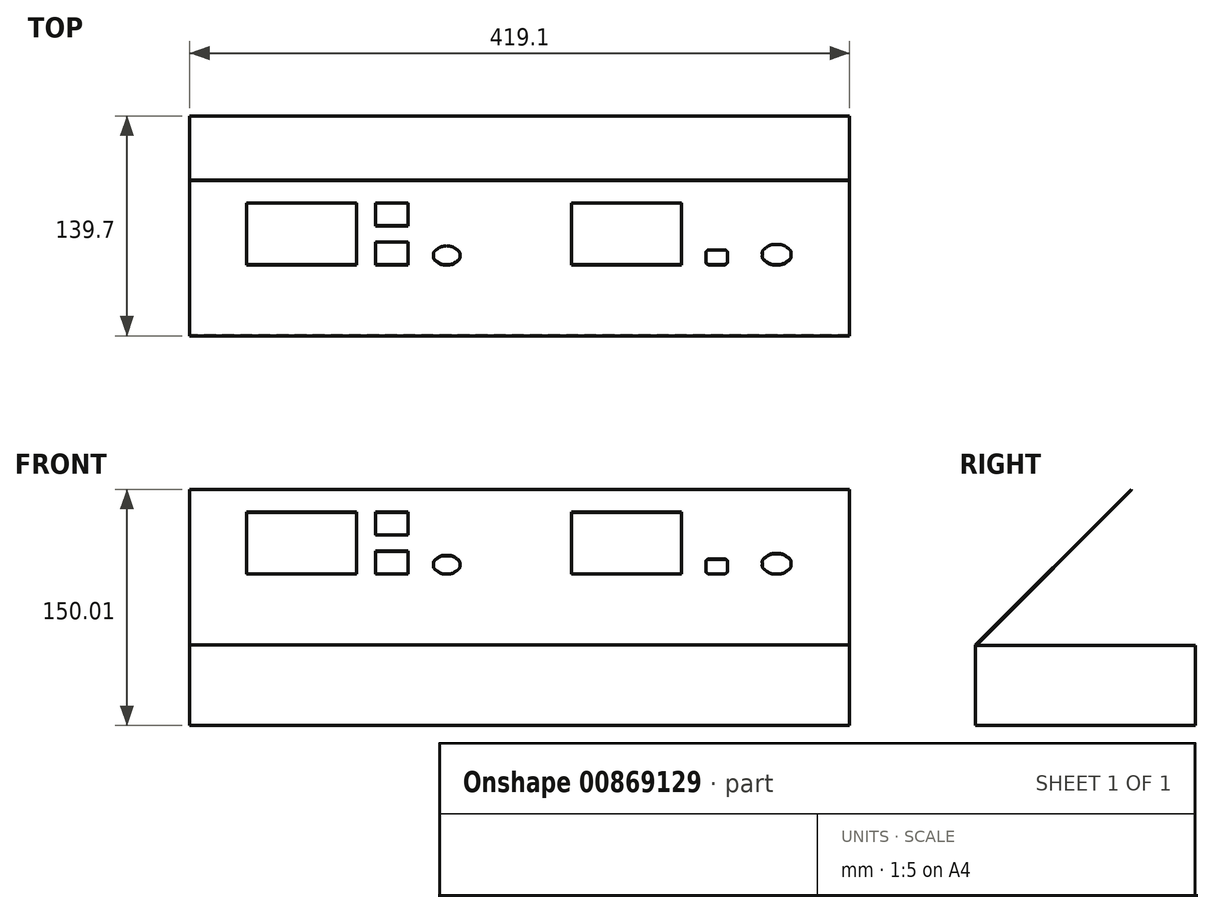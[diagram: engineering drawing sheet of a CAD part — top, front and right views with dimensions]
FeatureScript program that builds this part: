
annotation { "Feature Type Name" : "Feature", "Feature Type Description" : "" }
export const myFeature = defineFeature(function(context is Context, id is Id, definition is map)
    precondition{}
    {
        {
            var Q0;
            Q0=qCreatedBy(makeId("Right.planeOp"),FACE);
            var sketch = newSketch(context, id + "F0", { "sketchPlane" : qUnion([Q0])});
            skLineSegment(sketch, "E0.bottom", {"start": v(0, 0) * mm, "end": v(-139.7, 0) * mm});
            skLineSegment(sketch, "E0.top", {"start": v(0, 50.8) * mm, "end": v(-139.3, 50.8) * mm});
            skLineSegment(sketch, "E0.left", {"start": v(0, 0) * mm, "end": v(0, 50.8) * mm});
            skLineSegment(sketch, "E0.right", {"start": v(-139.7, 0) * mm, "end": v(-139.7, 51.22) * mm});
            skLineSegment(sketch, "E1", {"start": v(-139.7, 51.22) * mm, "end": v(-40.92, 150) * mm});
            skLineSegment(sketch, "E2", {"start": v(-40.92, 150) * mm, "end": v(-40.63, 149.72) * mm});
            skLineSegment(sketch, "E3", {"start": v(-40.63, 149.72) * mm, "end": v(-139.3, 51.05) * mm});
            skLineSegment(sketch, "E4", {"start": v(-139.3, 50.8) * mm, "end": v(-139.3, 51.05) * mm});
            skLineSegment(sketch, "E5", {"start": v(-139.3, 50.8) * mm, "end": v(-139.7, 50.8) * mm, "construction": true});
            skSolve(sketch);
        }
        {
            var Q0;
            Q0=qSketchRegion(id+"F0",true);
            extrude(context, id + "F1", {"entities" : qUnion([Q0]), "endBound" : BoundingType.SYMMETRIC, "depth" : 419.1 * mm, "offsetDistance" : 25.4 * mm});
        }
        {
            var Q0;
            Q0=makeQuery(id+"F1.opExtrude","SWEPT_FACE",FACE,{"disambiguationData":[OSD([sQuery(id+"F0.wireOp",EDGE,"E1")])]});
            var sketch = newSketch(context, id + "F2", { "sketchPlane" : qUnion([Q0])});
            skLineSegment(sketch, "E6", {"start": v(118.3, 12.35) * mm, "end": v(118.3, 3.62) * mm});
            skLineSegment(sketch, "E7", {"start": v(-173.4, 1.24) * mm, "end": v(-103.55, 1.24) * mm});
            skLineSegment(sketch, "E8", {"start": v(-173.4, 56.8) * mm, "end": v(-173.4, 1.24) * mm});
            skLineSegment(sketch, "E9", {"start": v(-103.55, 56.8) * mm, "end": v(-173.4, 56.8) * mm});
            skLineSegment(sketch, "E10", {"start": v(-103.55, 1.24) * mm, "end": v(-103.55, 56.8) * mm});
            skLineSegment(sketch, "E11", {"start": v(-71, 1.24) * mm, "end": v(-71, 21.88) * mm});
            skLineSegment(sketch, "E12", {"start": v(-91.64, 21.88) * mm, "end": v(-91.64, 1.24) * mm});
            skLineSegment(sketch, "E13", {"start": v(-91.64, 21.88) * mm, "end": v(-71, 21.88) * mm});
            skLineSegment(sketch, "E14", {"start": v(-91.64, 1.24) * mm, "end": v(-71, 1.24) * mm});
            skLineSegment(sketch, "E15", {"start": v(-91.64, 36.17) * mm, "end": v(-71, 36.17) * mm});
            skLineSegment(sketch, "E16", {"start": v(-91.64, 56.8) * mm, "end": v(-71, 56.8) * mm});
            skLineSegment(sketch, "E17", {"start": v(-91.64, 56.8) * mm, "end": v(-91.64, 36.17) * mm});
            skLineSegment(sketch, "E18", {"start": v(-71, 36.17) * mm, "end": v(-71, 56.8) * mm});
            skLineSegment(sketch, "E19", {"start": v(102.83, 1.24) * mm, "end": v(102.83, 56.8) * mm});
            skLineSegment(sketch, "E20", {"start": v(102.83, 56.8) * mm, "end": v(32.98, 56.8) * mm});
            skLineSegment(sketch, "E21", {"start": v(32.98, 56.8) * mm, "end": v(32.98, 1.24) * mm});
            skLineSegment(sketch, "E22", {"start": v(32.98, 1.24) * mm, "end": v(102.83, 1.24) * mm});
            skLineSegment(sketch, "E23", {"start": v(-209.9, -62.26) * mm, "end": v(-209.9, 76.65) * mm, "construction": true});
            skLineSegment(sketch, "E24", {"start": v(131.8, 3.62) * mm, "end": v(131.8, 12.35) * mm});
            skLineSegment(sketch, "E25", {"start": v(209.2, -62.26) * mm, "end": v(209.2, 76.65) * mm, "construction": true});
            skLineSegment(sketch, "E26", {"start": v(-209.9, 76.65) * mm, "end": v(209.2, 76.65) * mm, "construction": true});
            skLineSegment(sketch, "E27", {"start": v(129.42, 14.74) * mm, "end": v(120.69, 14.74) * mm});
            skLineSegment(sketch, "E28", {"start": v(120.69, 1.24) * mm, "end": v(129.42, 1.24) * mm});
            skLineSegment(sketch, "E29", {"start": v(209.2, -62.26) * mm, "end": v(-209.9, -62.26) * mm, "construction": true});
            skFitSpline(sketch, "E30", {"points": [v(120.69, 14.74) * mm, v(120.06, 14.74) * mm, v(119.44, 14.48) * mm, v(119, 14.04) * mm]});
            skFitSpline(sketch, "E31", {"points": [v(119, 14.04) * mm, v(118.56, 13.6) * mm, v(118.3, 12.98) * mm, v(118.3, 12.35) * mm]});
            skFitSpline(sketch, "E32", {"points": [v(-46.4, 17.91) * mm, v(-48.58, 17.91) * mm, v(-50.75, 17.01) * mm, v(-52.29, 15.47) * mm]});
            skFitSpline(sketch, "E33", {"points": [v(-52.29, 15.47) * mm, v(-53.83, 13.93) * mm, v(-54.73, 11.76) * mm, v(-54.73, 9.58) * mm, v(-54.73, 7.4) * mm, v(-53.83, 5.23) * mm, v(-52.29, 3.68) * mm]});
            skFitSpline(sketch, "E34", {"points": [v(-52.29, 3.68) * mm, v(-50.75, 2.14) * mm, v(-48.58, 1.24) * mm, v(-46.4, 1.24) * mm, v(-44.21, 1.24) * mm, v(-42.05, 2.14) * mm, v(-40.5, 3.68) * mm]});
            skFitSpline(sketch, "E35", {"points": [v(-40.5, 3.68) * mm, v(-38.96, 5.23) * mm, v(-38.06, 7.4) * mm, v(-38.06, 9.58) * mm, v(-38.06, 11.76) * mm, v(-38.96, 13.93) * mm, v(-40.5, 15.47) * mm]});
            skFitSpline(sketch, "E36", {"points": [v(-40.5, 15.47) * mm, v(-42.05, 17.01) * mm, v(-44.21, 17.91) * mm, v(-46.4, 17.91) * mm]});
            skFitSpline(sketch, "E37", {"points": [v(118.3, 3.62) * mm, v(118.3, 3) * mm, v(118.56, 2.38) * mm, v(119, 1.94) * mm]});
            skFitSpline(sketch, "E38", {"points": [v(119, 1.94) * mm, v(119.44, 1.5) * mm, v(120.06, 1.24) * mm, v(120.69, 1.24) * mm]});
            skFitSpline(sketch, "E39", {"points": [v(163.15, 19.5) * mm, v(160.76, 19.5) * mm, v(158.39, 18.51) * mm, v(156.7, 16.82) * mm]});
            skFitSpline(sketch, "E40", {"points": [v(156.7, 16.82) * mm, v(155, 15.14) * mm, v(154.03, 12.76) * mm, v(154.03, 10.37) * mm, v(154.03, 7.98) * mm, v(155, 5.6) * mm, v(156.7, 3.92) * mm]});
            skFitSpline(sketch, "E41", {"points": [v(156.7, 3.92) * mm, v(158.39, 2.23) * mm, v(160.76, 1.24) * mm, v(163.15, 1.24) * mm, v(165.54, 1.24) * mm, v(167.92, 2.23) * mm, v(169.6, 3.92) * mm]});
            skFitSpline(sketch, "E42", {"points": [v(169.6, 3.92) * mm, v(171.3, 5.6) * mm, v(172.28, 7.98) * mm, v(172.28, 10.37) * mm, v(172.28, 12.76) * mm, v(171.3, 15.14) * mm, v(169.6, 16.82) * mm]});
            skFitSpline(sketch, "E43", {"points": [v(169.6, 16.82) * mm, v(167.92, 18.51) * mm, v(165.54, 19.5) * mm, v(163.15, 19.5) * mm]});
            skFitSpline(sketch, "E44", {"points": [v(131.8, 12.35) * mm, v(131.8, 12.98) * mm, v(131.54, 13.6) * mm, v(131.1, 14.04) * mm]});
            skFitSpline(sketch, "E45", {"points": [v(131.1, 14.04) * mm, v(130.66, 14.48) * mm, v(130.04, 14.74) * mm, v(129.42, 14.74) * mm]});
            skFitSpline(sketch, "E46", {"points": [v(129.42, 1.24) * mm, v(130.04, 1.24) * mm, v(130.66, 1.5) * mm, v(131.1, 1.94) * mm]});
            skFitSpline(sketch, "E47", {"points": [v(131.1, 1.94) * mm, v(131.54, 2.38) * mm, v(131.8, 3) * mm, v(131.8, 3.62) * mm]});
            skFitSpline(sketch, "E48", {"points": [v(115.13, 3.62) * mm, v(115.13, 3.63) * mm, v(115.13, 3.63) * mm, v(115.13, 3.85) * mm, v(115.13, 12.35) * mm, v(115.13, 12.35) * mm, v(115.13, 12.36) * mm, v(115.13, 13.82) * mm, v(115.73, 15.25) * mm, v(116.76, 16.29) * mm]});
            skFitSpline(sketch, "E49", {"points": [v(116.76, 16.29) * mm, v(117.8, 17.32) * mm, v(119.22, 17.9) * mm, v(120.68, 17.91) * mm, v(120.69, 17.91) * mm, v(120.7, 17.91) * mm, v(128.15, 17.91) * mm, v(128.35, 17.91) * mm, v(128.35, 17.91) * mm, v(128.35, 17.91) * mm]});
            skSolve(sketch);
        }
        {
            var Q0;
            Q0=qSketchRegion(id+"F2",true);
            var Q1;
            Q1=makeQuery(id+"F1.opExtrude","SWEPT_FACE",FACE,{"disambiguationData":[OSD([sQuery(id+"F0.wireOp",EDGE,"E3")])]});
            extrude(context, id + "F3", {"entities" : qUnion([Q0]), "operationType" : NewBodyOperationType.REMOVE, "endBound" : BoundingType.UP_TO_SURFACE, "oppositeDirection" : true, "depth" : 25.4 * mm, "endBoundEntityFace" : qUnion([Q1]), "offsetDistance" : 25.4 * mm});
        }
    });
